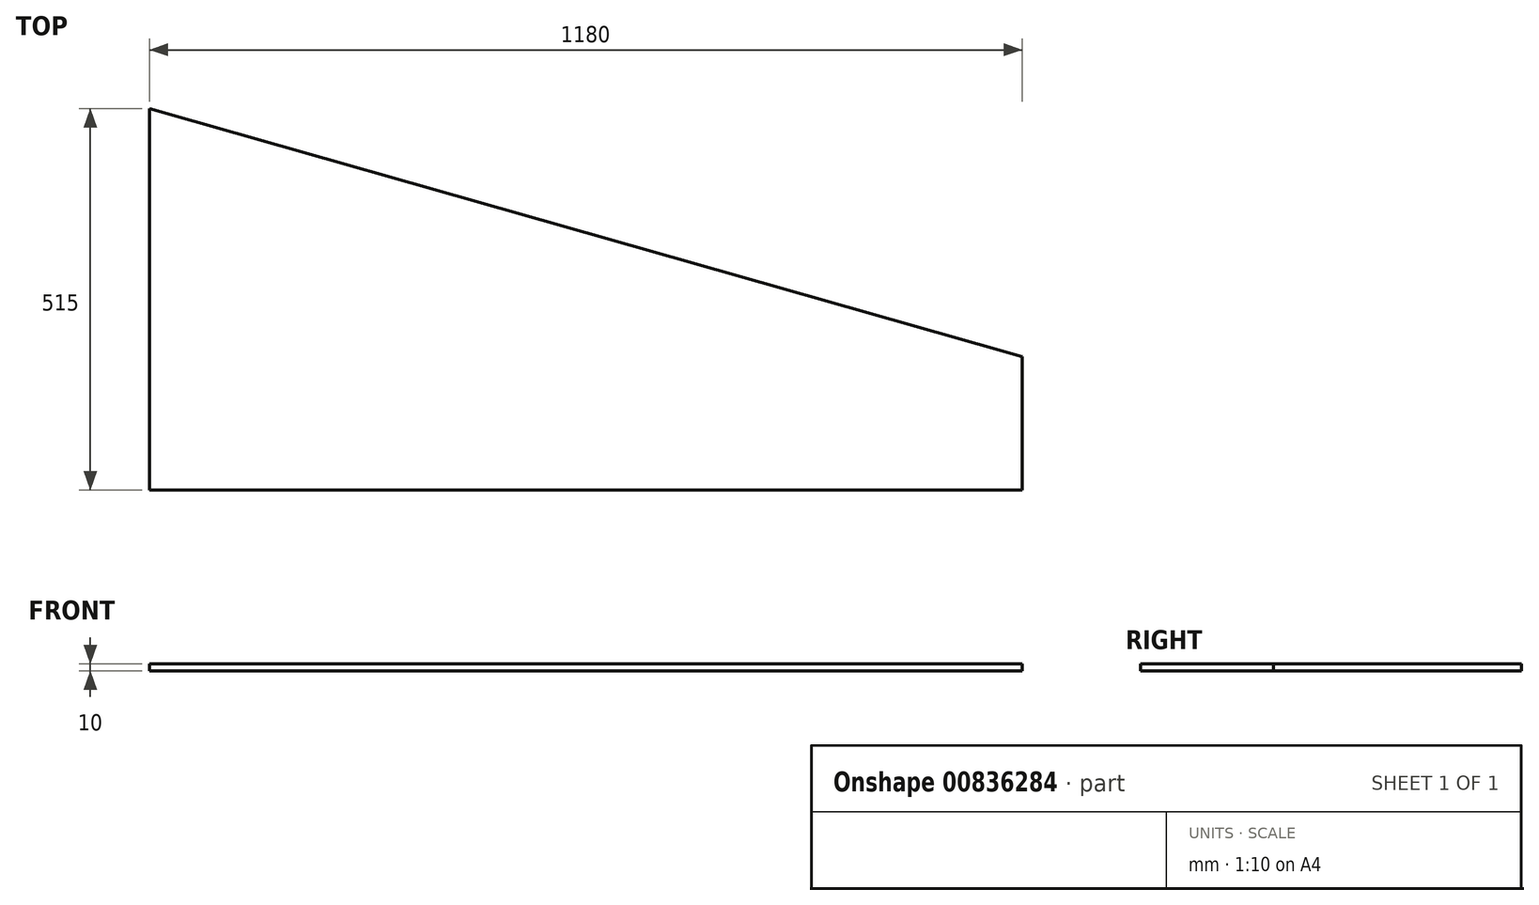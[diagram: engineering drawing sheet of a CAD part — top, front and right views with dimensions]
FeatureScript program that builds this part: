
annotation { "Feature Type Name" : "Feature", "Feature Type Description" : "" }
export const myFeature = defineFeature(function(context is Context, id is Id, definition is map)
    precondition{}
    {
        {
            var Q0;
            Q0=qCreatedBy(makeId("Top.planeOp"),FACE);
            var sketch = newSketch(context, id + "F0", { "sketchPlane" : qUnion([Q0])});
            skLineSegment(sketch, "E0.bottom", {"start": v(0, 0) * mm, "end": v(1180, 0) * mm});
            skLineSegment(sketch, "E0.left", {"start": v(0, 0) * mm, "end": v(0, 515) * mm});
            skLineSegment(sketch, "E1", {"start": v(1180, 0) * mm, "end": v(1180, 180) * mm});
            skLineSegment(sketch, "E2", {"start": v(1180, 180) * mm, "end": v(0, 515) * mm});
            skSolve(sketch);
        }
        {
            var Q0;
            Q0=makeQuery(id+"F0.imprint","IMPRINT",FACE,{"disambiguationData":[TD([[makeQuery(id+"F0.imprint","IMPRINT",EDGE,{"derivedFrom":sQuery(id+"F0.wireOp",EDGE,"E0.bottom")}),1.0]])]});
            extrude(context, id + "F1", {"entities" : qUnion([Q0]), "depth" : 10 * mm, "offsetDistance" : 25 * mm});
        }
    });
